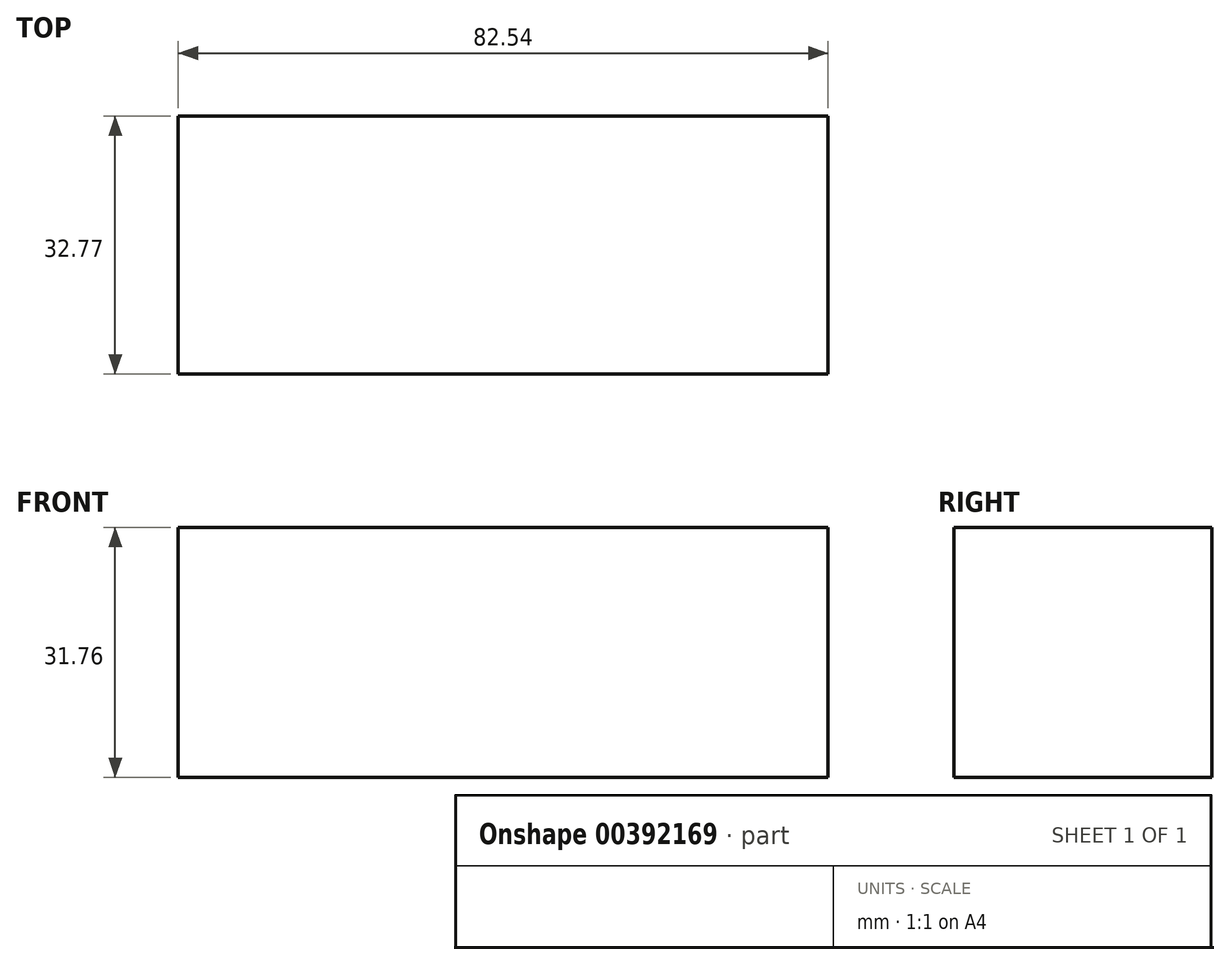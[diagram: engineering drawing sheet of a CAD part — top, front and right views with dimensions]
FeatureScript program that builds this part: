
annotation { "Feature Type Name" : "Feature", "Feature Type Description" : "" }
export const myFeature = defineFeature(function(context is Context, id is Id, definition is map)
    precondition{}
    {
        {
            var Q0;
            Q0=qCreatedBy(makeId("Front.planeOp"),FACE);
            var sketch = newSketch(context, id + "F0", { "sketchPlane" : qUnion([Q0])});
            skLineSegment(sketch, "E0.bottom", {"start": v(41.28, 15.88) * mm, "end": v(-41.28, 15.88) * mm});
            skLineSegment(sketch, "E0.top", {"start": v(41.28, -15.88) * mm, "end": v(-41.28, -15.88) * mm});
            skLineSegment(sketch, "E0.left", {"start": v(41.28, 15.88) * mm, "end": v(41.28, -15.88) * mm});
            skLineSegment(sketch, "E0.right", {"start": v(-41.28, 15.88) * mm, "end": v(-41.28, -15.88) * mm});
            skPoint(sketch, "E0.middle", {"position": v(0, 0) * mm});
            skSolve(sketch);
        }
        {
            var Q0;
            Q0 = qSketchRegion(id + "F0", true);
            extrude(context, id + "F1", {"entities" : qUnion([Q0]), "depth" : 32.77 * mm});
        }
    });
